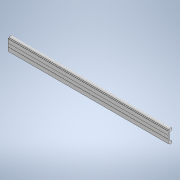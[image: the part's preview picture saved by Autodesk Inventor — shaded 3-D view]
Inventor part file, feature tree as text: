
AUTODESK INVENTOR PART (.ipt)
format: ipt  version: 2020 (Build 240168000, 168)  size: 121,344 bytes
history: native  units: mm
features: other x1, extrude x1, sketch x1
ambient origin geometry x8: Origin, YZ Plane, XZ Plane, XY Plane, X Axis, Y Axis, Z Axis, Center Point
bodies: Body1 (feature_tree)
feature tree (3):
  other  "Bryła1"
  extrude  "Wyciągnięcie proste1"  Depth=574.0mm TaperAngle=0.0deg
  sketch  "Szkic1"
